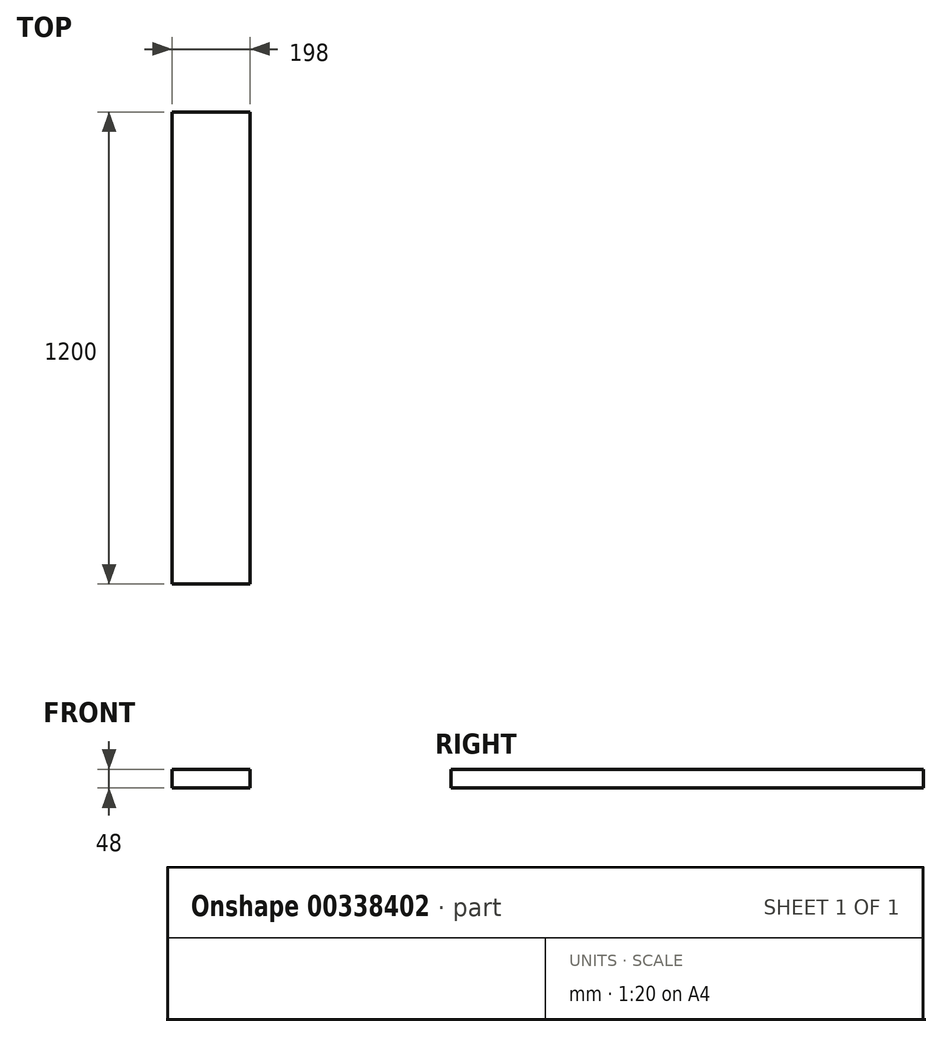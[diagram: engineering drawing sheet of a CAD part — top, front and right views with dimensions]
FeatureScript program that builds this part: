
annotation { "Feature Type Name" : "Feature", "Feature Type Description" : "" }
export const myFeature = defineFeature(function(context is Context, id is Id, definition is map)
    precondition{}
    {
        {
            var Q0;
            Q0=qCreatedBy(makeId("Front.planeOp"),FACE);
            var sketch = newSketch(context, id + "F0", { "sketchPlane" : qUnion([Q0])});
            skLineSegment(sketch, "E0.bottom", {"start": v(-99, -24) * mm, "end": v(99, -24) * mm});
            skLineSegment(sketch, "E0.top", {"start": v(-99, 24) * mm, "end": v(99, 24) * mm});
            skLineSegment(sketch, "E0.left", {"start": v(-99, -24) * mm, "end": v(-99, 24) * mm});
            skLineSegment(sketch, "E0.right", {"start": v(99, -24) * mm, "end": v(99, 24) * mm});
            skPoint(sketch, "E0.middle", {"position": v(0, 0) * mm});
            skSolve(sketch);
        }
        {
            var Q0;
            Q0=makeQuery(id+"F0.imprint","IMPRINT",FACE,{"disambiguationData":[TD([[makeQuery(id+"F0.imprint","IMPRINT",EDGE,{"derivedFrom":sQuery(id+"F0.wireOp",EDGE,"E0.bottom")}),1.0]])]});
            extrude(context, id + "F1", {"entities" : qUnion([Q0]), "offsetDistance" : 25 * mm, "depth" : 1200 * mm});
        }
    });
